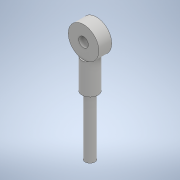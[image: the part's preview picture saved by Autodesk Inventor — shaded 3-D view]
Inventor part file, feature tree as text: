
AUTODESK INVENTOR PART (.ipt)
format: ipt  version: 2020.2 (Build 242310000, 310)  size: 129,024 bytes
history: native  units: mm
features: sketch x5, extrude x5, other x3, hole x1
ambient origin geometry x8: Origin, YZ Plane, XZ Plane, XY Plane, X Axis, Y Axis, Z Axis, Center Point
bodies: Body1 (feature_tree)
feature tree (14):
  other  "ソリッド1"
  sketch  "スケッチ1"
  extrude  "押し出し1"  Depth=3.0mm
  extrude  "押し出し2"  Depth=5.0mm
  other  "作業平面1"
  sketch  "スケッチ2"
  extrude  "押し出し3"  Depth=14.0mm TaperAngle=0.0deg
  extrude  "押し出し4"  Depth=18.5mm TaperAngle=0.0deg
  sketch  "スケッチ4"
  extrude  "押し出し5"  Depth=9.5mm
  hole  "穴1"  [1 undecoded]
  sketch  "スケッチ5"
  sketch  "スケッチ3"
  other  "断面エッジを投影1"
note: 1 required parameter value undecoded (feature->parameter linkage not recoverable at this tier; creation-order binding heuristic only, values carry confidence <= 0.55)
